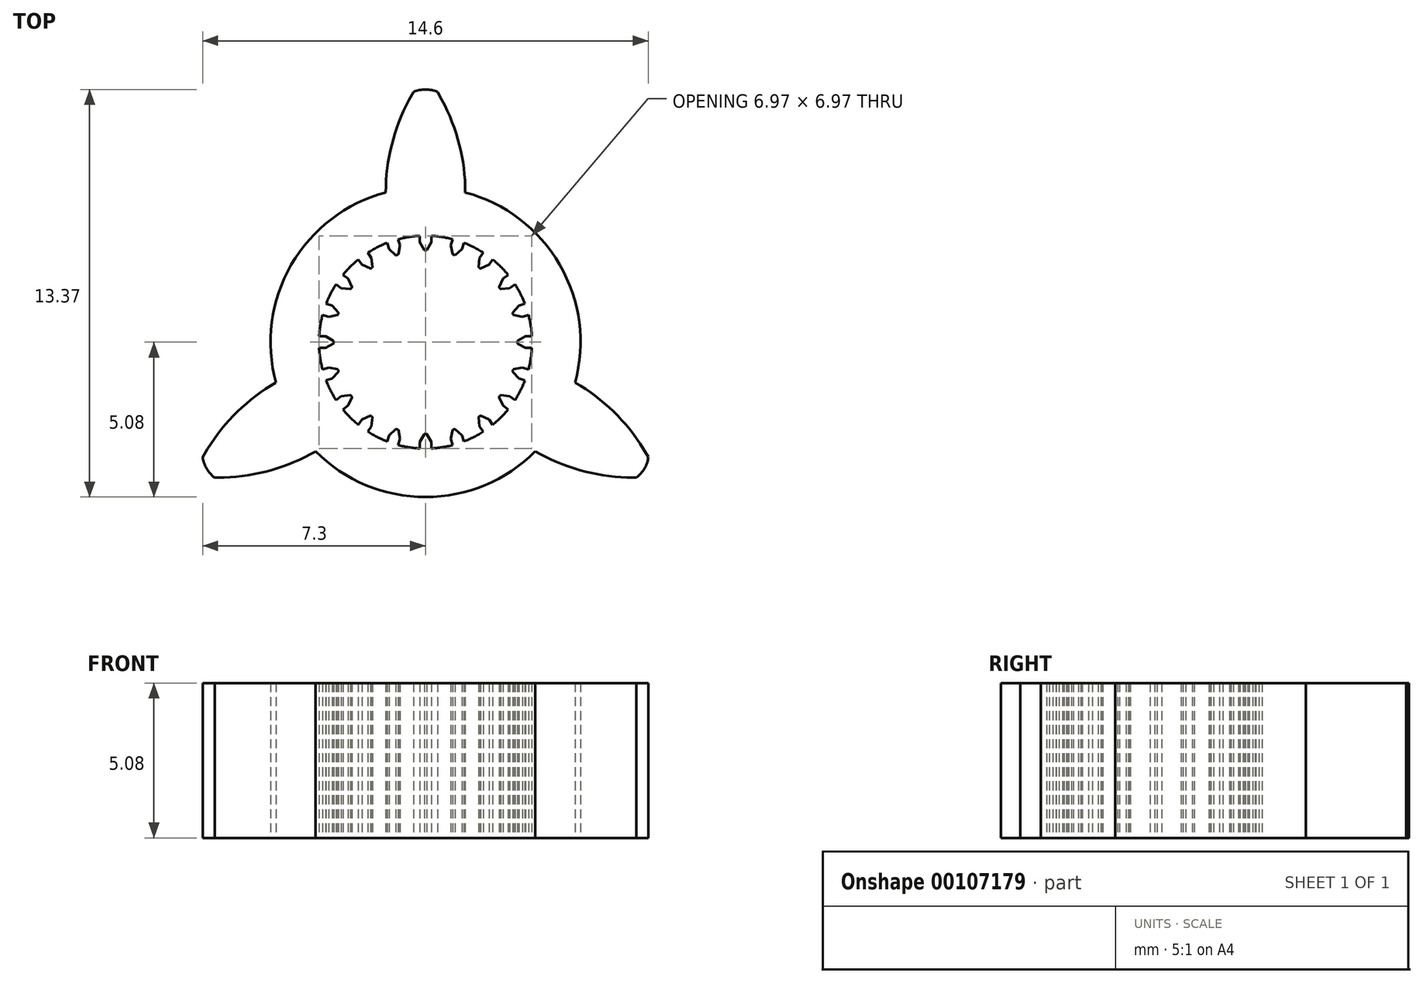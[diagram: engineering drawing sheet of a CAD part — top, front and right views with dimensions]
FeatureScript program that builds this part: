
annotation { "Feature Type Name" : "Feature", "Feature Type Description" : "" }
export const myFeature = defineFeature(function(context is Context, id is Id, definition is map)
    precondition{}
    {
        {
            var Q0;
            Q0=qCreatedBy(makeId("Top.planeOp"),FACE);
            var sketch = newSketch(context, id + "F0", { "sketchPlane" : qUnion([Q0])});
            skArc(sketch, "E0", {"start": v(-1.3, 4.9) * mm, "mid": v(-4.4, 2.54) * mm, "end": v(-4.9, -1.33) * mm});
            skLineSegment(sketch, "E1", {"start": v(-0.2, 3.49) * mm, "end": v(-0.2, 3.28) * mm});
            skArc(sketch, "E2", {"start": v(-0.04, 3.02) * mm, "mid": v(0, 3) * mm, "end": v(0.04, 3.02) * mm});
            skLineSegment(sketch, "E3", {"start": v(-0.2, 3.28) * mm, "end": v(-0.04, 3.02) * mm});
            skLineSegment(sketch, "E4.MirrorCS", {"start": v(0.2, 3.49) * mm, "end": v(0.2, 3.28) * mm});
            skLineSegment(sketch, "E5.MirrorCS", {"start": v(0.2, 3.28) * mm, "end": v(0.04, 3.02) * mm});
            skLineSegment(sketch, "E6.1.0", {"start": v(-0.9, 3.38) * mm, "end": v(-0.83, 3.18) * mm});
            skLineSegment(sketch, "E6.1.1", {"start": v(-0.83, 3.18) * mm, "end": v(-0.9, 2.88) * mm});
            skArc(sketch, "E6.1.2", {"start": v(-0.97, 2.85) * mm, "mid": v(-0.93, 2.86) * mm, "end": v(-0.9, 2.88) * mm});
            skLineSegment(sketch, "E6.1.3", {"start": v(-1.2, 3.06) * mm, "end": v(-0.97, 2.85) * mm});
            skLineSegment(sketch, "E6.1.4", {"start": v(-1.26, 3.26) * mm, "end": v(-1.2, 3.06) * mm});
            skLineSegment(sketch, "E6.2.0", {"start": v(-1.9, 2.93) * mm, "end": v(-1.77, 2.76) * mm});
            skLineSegment(sketch, "E6.2.1", {"start": v(-1.77, 2.76) * mm, "end": v(-1.74, 2.47) * mm});
            skArc(sketch, "E6.2.2", {"start": v(-1.8, 2.41) * mm, "mid": v(-1.77, 2.43) * mm, "end": v(-1.74, 2.47) * mm});
            skLineSegment(sketch, "E6.2.3", {"start": v(-2.08, 2.54) * mm, "end": v(-1.8, 2.41) * mm});
            skLineSegment(sketch, "E6.2.4", {"start": v(-2.2, 2.7) * mm, "end": v(-2.08, 2.54) * mm});
            skLineSegment(sketch, "E6.3.0", {"start": v(-2.7, 2.2) * mm, "end": v(-2.54, 2.08) * mm});
            skLineSegment(sketch, "E6.3.1", {"start": v(-2.54, 2.08) * mm, "end": v(-2.41, 1.8) * mm});
            skArc(sketch, "E6.3.2", {"start": v(-2.47, 1.74) * mm, "mid": v(-2.43, 1.77) * mm, "end": v(-2.41, 1.8) * mm});
            skLineSegment(sketch, "E6.3.3", {"start": v(-2.76, 1.77) * mm, "end": v(-2.47, 1.74) * mm});
            skLineSegment(sketch, "E6.3.4", {"start": v(-2.93, 1.9) * mm, "end": v(-2.76, 1.77) * mm});
            skLineSegment(sketch, "E6.4.0", {"start": v(-3.26, 1.26) * mm, "end": v(-3.06, 1.2) * mm});
            skLineSegment(sketch, "E6.4.1", {"start": v(-3.06, 1.2) * mm, "end": v(-2.85, 0.97) * mm});
            skArc(sketch, "E6.4.2", {"start": v(-2.88, 0.9) * mm, "mid": v(-2.86, 0.93) * mm, "end": v(-2.85, 0.97) * mm});
            skLineSegment(sketch, "E6.4.3", {"start": v(-3.18, 0.83) * mm, "end": v(-2.88, 0.9) * mm});
            skLineSegment(sketch, "E6.4.4", {"start": v(-3.38, 0.9) * mm, "end": v(-3.18, 0.83) * mm});
            skLineSegment(sketch, "E6.5.0", {"start": v(-3.49, 0.2) * mm, "end": v(-3.28, 0.2) * mm});
            skLineSegment(sketch, "E6.5.1", {"start": v(-3.28, 0.2) * mm, "end": v(-3.02, 0.04) * mm});
            skArc(sketch, "E6.5.2", {"start": v(-3.02, -0.04) * mm, "mid": v(-3, 0) * mm, "end": v(-3.02, 0.04) * mm});
            skLineSegment(sketch, "E6.5.3", {"start": v(-3.28, -0.2) * mm, "end": v(-3.02, -0.04) * mm});
            skLineSegment(sketch, "E6.5.4", {"start": v(-3.49, -0.2) * mm, "end": v(-3.28, -0.2) * mm});
            skLineSegment(sketch, "E6.6.0", {"start": v(-3.38, -0.9) * mm, "end": v(-3.18, -0.83) * mm});
            skLineSegment(sketch, "E6.6.1", {"start": v(-3.18, -0.83) * mm, "end": v(-2.88, -0.9) * mm});
            skArc(sketch, "E6.6.2", {"start": v(-2.85, -0.97) * mm, "mid": v(-2.86, -0.93) * mm, "end": v(-2.88, -0.9) * mm});
            skLineSegment(sketch, "E6.6.3", {"start": v(-3.06, -1.2) * mm, "end": v(-2.85, -0.97) * mm});
            skLineSegment(sketch, "E6.6.4", {"start": v(-3.26, -1.26) * mm, "end": v(-3.06, -1.2) * mm});
            skLineSegment(sketch, "E6.7.0", {"start": v(-2.93, -1.9) * mm, "end": v(-2.76, -1.77) * mm});
            skLineSegment(sketch, "E6.7.1", {"start": v(-2.76, -1.77) * mm, "end": v(-2.47, -1.74) * mm});
            skArc(sketch, "E6.7.2", {"start": v(-2.41, -1.8) * mm, "mid": v(-2.43, -1.77) * mm, "end": v(-2.47, -1.74) * mm});
            skLineSegment(sketch, "E6.7.3", {"start": v(-2.54, -2.08) * mm, "end": v(-2.41, -1.8) * mm});
            skLineSegment(sketch, "E6.7.4", {"start": v(-2.7, -2.2) * mm, "end": v(-2.54, -2.08) * mm});
            skLineSegment(sketch, "E6.8.0", {"start": v(-2.2, -2.7) * mm, "end": v(-2.08, -2.54) * mm});
            skLineSegment(sketch, "E6.8.1", {"start": v(-2.08, -2.54) * mm, "end": v(-1.8, -2.41) * mm});
            skArc(sketch, "E6.8.2", {"start": v(-1.74, -2.47) * mm, "mid": v(-1.77, -2.43) * mm, "end": v(-1.8, -2.41) * mm});
            skLineSegment(sketch, "E6.8.3", {"start": v(-1.77, -2.76) * mm, "end": v(-1.74, -2.47) * mm});
            skLineSegment(sketch, "E6.8.4", {"start": v(-1.9, -2.93) * mm, "end": v(-1.77, -2.76) * mm});
            skLineSegment(sketch, "E6.9.0", {"start": v(-1.26, -3.26) * mm, "end": v(-1.2, -3.06) * mm});
            skLineSegment(sketch, "E6.9.1", {"start": v(-1.2, -3.06) * mm, "end": v(-0.97, -2.85) * mm});
            skArc(sketch, "E6.9.2", {"start": v(-0.9, -2.88) * mm, "mid": v(-0.93, -2.86) * mm, "end": v(-0.97, -2.85) * mm});
            skLineSegment(sketch, "E6.9.3", {"start": v(-0.83, -3.18) * mm, "end": v(-0.9, -2.88) * mm});
            skLineSegment(sketch, "E6.9.4", {"start": v(-0.9, -3.38) * mm, "end": v(-0.83, -3.18) * mm});
            skLineSegment(sketch, "E6.10.0", {"start": v(-0.2, -3.49) * mm, "end": v(-0.2, -3.28) * mm});
            skLineSegment(sketch, "E6.10.1", {"start": v(-0.2, -3.28) * mm, "end": v(-0.04, -3.02) * mm});
            skArc(sketch, "E6.10.2", {"start": v(0.04, -3.02) * mm, "mid": v(0, -3) * mm, "end": v(-0.04, -3.02) * mm});
            skLineSegment(sketch, "E6.10.3", {"start": v(0.2, -3.28) * mm, "end": v(0.04, -3.02) * mm});
            skLineSegment(sketch, "E6.10.4", {"start": v(0.2, -3.49) * mm, "end": v(0.2, -3.28) * mm});
            skLineSegment(sketch, "E6.11.0", {"start": v(0.9, -3.38) * mm, "end": v(0.83, -3.18) * mm});
            skLineSegment(sketch, "E6.11.1", {"start": v(0.83, -3.18) * mm, "end": v(0.9, -2.88) * mm});
            skArc(sketch, "E6.11.2", {"start": v(0.97, -2.85) * mm, "mid": v(0.93, -2.86) * mm, "end": v(0.9, -2.88) * mm});
            skLineSegment(sketch, "E6.11.3", {"start": v(1.2, -3.06) * mm, "end": v(0.97, -2.85) * mm});
            skLineSegment(sketch, "E6.11.4", {"start": v(1.26, -3.26) * mm, "end": v(1.2, -3.06) * mm});
            skLineSegment(sketch, "E6.12.0", {"start": v(1.9, -2.93) * mm, "end": v(1.77, -2.76) * mm});
            skLineSegment(sketch, "E6.12.1", {"start": v(1.77, -2.76) * mm, "end": v(1.74, -2.47) * mm});
            skArc(sketch, "E6.12.2", {"start": v(1.8, -2.41) * mm, "mid": v(1.77, -2.43) * mm, "end": v(1.74, -2.47) * mm});
            skLineSegment(sketch, "E6.12.3", {"start": v(2.08, -2.54) * mm, "end": v(1.8, -2.41) * mm});
            skLineSegment(sketch, "E6.12.4", {"start": v(2.2, -2.7) * mm, "end": v(2.08, -2.54) * mm});
            skLineSegment(sketch, "E6.13.0", {"start": v(2.7, -2.2) * mm, "end": v(2.54, -2.08) * mm});
            skLineSegment(sketch, "E6.13.1", {"start": v(2.54, -2.08) * mm, "end": v(2.41, -1.8) * mm});
            skArc(sketch, "E6.13.2", {"start": v(2.47, -1.74) * mm, "mid": v(2.43, -1.77) * mm, "end": v(2.41, -1.8) * mm});
            skLineSegment(sketch, "E6.13.3", {"start": v(2.76, -1.77) * mm, "end": v(2.47, -1.74) * mm});
            skLineSegment(sketch, "E6.13.4", {"start": v(2.93, -1.9) * mm, "end": v(2.76, -1.77) * mm});
            skLineSegment(sketch, "E6.14.0", {"start": v(3.26, -1.26) * mm, "end": v(3.06, -1.2) * mm});
            skLineSegment(sketch, "E6.14.1", {"start": v(3.06, -1.2) * mm, "end": v(2.85, -0.97) * mm});
            skArc(sketch, "E6.14.2", {"start": v(2.88, -0.9) * mm, "mid": v(2.86, -0.93) * mm, "end": v(2.85, -0.97) * mm});
            skLineSegment(sketch, "E6.14.3", {"start": v(3.18, -0.83) * mm, "end": v(2.88, -0.9) * mm});
            skLineSegment(sketch, "E6.14.4", {"start": v(3.38, -0.9) * mm, "end": v(3.18, -0.83) * mm});
            skLineSegment(sketch, "E6.15.0", {"start": v(3.49, -0.2) * mm, "end": v(3.28, -0.2) * mm});
            skLineSegment(sketch, "E6.15.1", {"start": v(3.28, -0.2) * mm, "end": v(3.02, -0.04) * mm});
            skArc(sketch, "E6.15.2", {"start": v(3.02, 0.04) * mm, "mid": v(3, 0) * mm, "end": v(3.02, -0.04) * mm});
            skLineSegment(sketch, "E6.15.3", {"start": v(3.28, 0.2) * mm, "end": v(3.02, 0.04) * mm});
            skLineSegment(sketch, "E6.15.4", {"start": v(3.49, 0.2) * mm, "end": v(3.28, 0.2) * mm});
            skLineSegment(sketch, "E6.16.0", {"start": v(3.38, 0.9) * mm, "end": v(3.18, 0.83) * mm});
            skLineSegment(sketch, "E6.16.1", {"start": v(3.18, 0.83) * mm, "end": v(2.88, 0.9) * mm});
            skArc(sketch, "E6.16.2", {"start": v(2.85, 0.97) * mm, "mid": v(2.86, 0.93) * mm, "end": v(2.88, 0.9) * mm});
            skLineSegment(sketch, "E6.16.3", {"start": v(3.06, 1.2) * mm, "end": v(2.85, 0.97) * mm});
            skLineSegment(sketch, "E6.16.4", {"start": v(3.26, 1.26) * mm, "end": v(3.06, 1.2) * mm});
            skLineSegment(sketch, "E6.17.0", {"start": v(2.93, 1.9) * mm, "end": v(2.76, 1.77) * mm});
            skLineSegment(sketch, "E6.17.1", {"start": v(2.76, 1.77) * mm, "end": v(2.47, 1.74) * mm});
            skArc(sketch, "E6.17.2", {"start": v(2.41, 1.8) * mm, "mid": v(2.43, 1.77) * mm, "end": v(2.47, 1.74) * mm});
            skLineSegment(sketch, "E6.17.3", {"start": v(2.54, 2.08) * mm, "end": v(2.41, 1.8) * mm});
            skLineSegment(sketch, "E6.17.4", {"start": v(2.7, 2.2) * mm, "end": v(2.54, 2.08) * mm});
            skLineSegment(sketch, "E6.18.0", {"start": v(2.2, 2.7) * mm, "end": v(2.08, 2.54) * mm});
            skLineSegment(sketch, "E6.18.1", {"start": v(2.08, 2.54) * mm, "end": v(1.8, 2.41) * mm});
            skArc(sketch, "E6.18.2", {"start": v(1.74, 2.47) * mm, "mid": v(1.77, 2.43) * mm, "end": v(1.8, 2.41) * mm});
            skLineSegment(sketch, "E6.18.3", {"start": v(1.77, 2.76) * mm, "end": v(1.74, 2.47) * mm});
            skLineSegment(sketch, "E6.18.4", {"start": v(1.9, 2.93) * mm, "end": v(1.77, 2.76) * mm});
            skLineSegment(sketch, "E6.19.0", {"start": v(1.26, 3.26) * mm, "end": v(1.2, 3.06) * mm});
            skLineSegment(sketch, "E6.19.1", {"start": v(1.2, 3.06) * mm, "end": v(0.97, 2.85) * mm});
            skArc(sketch, "E6.19.2", {"start": v(0.9, 2.88) * mm, "mid": v(0.93, 2.86) * mm, "end": v(0.97, 2.85) * mm});
            skLineSegment(sketch, "E6.19.3", {"start": v(0.83, 3.18) * mm, "end": v(0.9, 2.88) * mm});
            skLineSegment(sketch, "E6.19.4", {"start": v(0.9, 3.38) * mm, "end": v(0.83, 3.18) * mm});
            skArc(sketch, "E7", {"start": v(0.2, 3.49) * mm, "mid": v(0.55, 3.45) * mm, "end": v(0.9, 3.38) * mm});
            skArc(sketch, "E8", {"start": v(3.38, 0.9) * mm, "mid": v(3.45, 0.55) * mm, "end": v(3.49, 0.2) * mm});
            skArc(sketch, "E9.1.0", {"start": v(2.93, 1.9) * mm, "mid": v(3.11, 1.59) * mm, "end": v(3.26, 1.26) * mm});
            skArc(sketch, "E9.2.0", {"start": v(2.2, 2.7) * mm, "mid": v(2.47, 2.47) * mm, "end": v(2.7, 2.2) * mm});
            skArc(sketch, "E9.3.0", {"start": v(1.26, 3.26) * mm, "mid": v(1.59, 3.11) * mm, "end": v(1.9, 2.93) * mm});
            skArc(sketch, "E9.5.0", {"start": v(-0.9, 3.38) * mm, "mid": v(-0.55, 3.45) * mm, "end": v(-0.2, 3.49) * mm});
            skArc(sketch, "E9.6.0", {"start": v(-1.9, 2.93) * mm, "mid": v(-1.59, 3.11) * mm, "end": v(-1.26, 3.26) * mm});
            skArc(sketch, "E9.7.0", {"start": v(-2.7, 2.2) * mm, "mid": v(-2.47, 2.47) * mm, "end": v(-2.2, 2.7) * mm});
            skArc(sketch, "E9.8.0", {"start": v(-3.26, 1.26) * mm, "mid": v(-3.11, 1.59) * mm, "end": v(-2.93, 1.9) * mm});
            skArc(sketch, "E9.9.0", {"start": v(-3.49, 0.2) * mm, "mid": v(-3.45, 0.55) * mm, "end": v(-3.38, 0.9) * mm});
            skArc(sketch, "E9.10.0", {"start": v(-3.38, -0.9) * mm, "mid": v(-3.45, -0.55) * mm, "end": v(-3.49, -0.2) * mm});
            skArc(sketch, "E9.11.0", {"start": v(-2.93, -1.9) * mm, "mid": v(-3.11, -1.59) * mm, "end": v(-3.26, -1.26) * mm});
            skArc(sketch, "E9.12.0", {"start": v(-2.2, -2.7) * mm, "mid": v(-2.47, -2.47) * mm, "end": v(-2.7, -2.2) * mm});
            skArc(sketch, "E9.13.0", {"start": v(-1.26, -3.26) * mm, "mid": v(-1.59, -3.11) * mm, "end": v(-1.9, -2.93) * mm});
            skArc(sketch, "E9.14.0", {"start": v(-0.2, -3.49) * mm, "mid": v(-0.55, -3.45) * mm, "end": v(-0.9, -3.38) * mm});
            skArc(sketch, "E9.15.0", {"start": v(0.9, -3.38) * mm, "mid": v(0.55, -3.45) * mm, "end": v(0.2, -3.49) * mm});
            skArc(sketch, "E9.16.0", {"start": v(1.9, -2.93) * mm, "mid": v(1.59, -3.11) * mm, "end": v(1.26, -3.26) * mm});
            skArc(sketch, "E9.17.0", {"start": v(2.7, -2.2) * mm, "mid": v(2.47, -2.47) * mm, "end": v(2.2, -2.7) * mm});
            skArc(sketch, "E9.18.0", {"start": v(3.26, -1.26) * mm, "mid": v(3.11, -1.59) * mm, "end": v(2.93, -1.9) * mm});
            skArc(sketch, "E9.19.0", {"start": v(3.49, -0.2) * mm, "mid": v(3.45, -0.55) * mm, "end": v(3.38, -0.9) * mm});
            skLineSegment(sketch, "E10", {"start": v(1.3, 4.9) * mm, "end": v(1.3, 4.92) * mm});
            skArc(sketch, "E11", {"start": v(0.4, 8.2) * mm, "mid": v(0.2, 8.27) * mm, "end": v(0, 8.29) * mm});
            skPoint(sketch, "E11.centerSnap0", {"position": v(0, 4.9) * mm});
            skLineSegment(sketch, "E12", {"start": v(0.54, 7.94) * mm, "end": v(0.4, 8.2) * mm});
            skPoint(sketch, "E13.visualSharp", {"position": v(1.3, 6.52) * mm});
            skArc(sketch, "E13.filletArc", {"start": v(1.3, 4.92) * mm, "mid": v(1.1, 6.47) * mm, "end": v(0.54, 7.94) * mm});
            skLineSegment(sketch, "E14.MirrorCS", {"start": v(-0.54, 7.94) * mm, "end": v(-0.4, 8.2) * mm});
            skLineSegment(sketch, "E15.MirrorCS", {"start": v(-1.3, 4.9) * mm, "end": v(-1.3, 4.92) * mm});
            skArc(sketch, "E16.MirrorCS", {"start": v(-0.4, 8.2) * mm, "mid": v(-0.2, 8.27) * mm, "end": v(0, 8.29) * mm});
            skPoint(sketch, "E17.MirrorP", {"position": v(-1.3, 6.52) * mm});
            skArc(sketch, "E18.MirrorCS", {"start": v(-1.3, 4.92) * mm, "mid": v(-1.1, 6.47) * mm, "end": v(-0.54, 7.94) * mm});
            skPoint(sketch, "E19.1.0", {"position": v(-4.25, -2.45) * mm});
            skPoint(sketch, "E19.1.1", {"position": v(-6.3, -2.13) * mm});
            skPoint(sketch, "E19.1.2", {"position": v(-5, -4.39) * mm});
            skArc(sketch, "E19.1.3", {"start": v(-3.6, -3.59) * mm, "mid": v(-5.05, -4.2) * mm, "end": v(-6.6, -4.43) * mm});
            skArc(sketch, "E19.1.4", {"start": v(-4.9, -1.33) * mm, "mid": v(-6.16, -2.28) * mm, "end": v(-7.14, -3.5) * mm});
            skPoint(sketch, "E19.1.5", {"position": v(-4.25, -2.45) * mm});
            skLineSegment(sketch, "E19.1.6", {"start": v(-7.14, -3.5) * mm, "end": v(-7.3, -3.77) * mm});
            skArc(sketch, "E19.1.7", {"start": v(-7.3, -3.77) * mm, "mid": v(-7.26, -3.96) * mm, "end": v(-7.18, -4.14) * mm});
            skArc(sketch, "E19.1.8", {"start": v(-6.91, -4.44) * mm, "mid": v(-7.06, -4.3) * mm, "end": v(-7.18, -4.14) * mm});
            skLineSegment(sketch, "E19.1.9", {"start": v(-6.6, -4.43) * mm, "end": v(-6.91, -4.44) * mm});
            skLineSegment(sketch, "E19.1.10", {"start": v(-4.9, -1.33) * mm, "end": v(-4.9, -1.33) * mm});
            skLineSegment(sketch, "E19.1.11", {"start": v(-3.6, -3.58) * mm, "end": v(-3.6, -3.59) * mm});
            skPoint(sketch, "E19.2.0", {"position": v(4.25, -2.45) * mm});
            skPoint(sketch, "E19.2.1", {"position": v(5, -4.39) * mm});
            skPoint(sketch, "E19.2.2", {"position": v(6.3, -2.13) * mm});
            skArc(sketch, "E19.2.3", {"start": v(4.9, -1.33) * mm, "mid": v(6.16, -2.28) * mm, "end": v(7.14, -3.5) * mm});
            skArc(sketch, "E19.2.4", {"start": v(3.6, -3.59) * mm, "mid": v(5.05, -4.2) * mm, "end": v(6.6, -4.43) * mm});
            skPoint(sketch, "E19.2.5", {"position": v(4.25, -2.45) * mm});
            skLineSegment(sketch, "E19.2.6", {"start": v(6.6, -4.43) * mm, "end": v(6.91, -4.44) * mm});
            skArc(sketch, "E19.2.7", {"start": v(6.91, -4.44) * mm, "mid": v(7.06, -4.3) * mm, "end": v(7.18, -4.14) * mm});
            skArc(sketch, "E19.2.8", {"start": v(7.3, -3.77) * mm, "mid": v(7.26, -3.96) * mm, "end": v(7.18, -4.14) * mm});
            skLineSegment(sketch, "E19.2.9", {"start": v(7.14, -3.5) * mm, "end": v(7.3, -3.77) * mm});
            skLineSegment(sketch, "E19.2.10", {"start": v(3.6, -3.58) * mm, "end": v(3.6, -3.59) * mm});
            skLineSegment(sketch, "E19.2.11", {"start": v(4.9, -1.33) * mm, "end": v(4.9, -1.33) * mm});
            skArc(sketch, "E20.trimOffspring", {"start": v(4.9, -1.33) * mm, "mid": v(4.4, 2.54) * mm, "end": v(1.3, 4.9) * mm});
            skArc(sketch, "E21.trimOffspring", {"start": v(-3.6, -3.58) * mm, "mid": v(0, -5.08) * mm, "end": v(3.6, -3.58) * mm});
            skSolve(sketch);
        }
        {
            var Q0;
            Q0=makeQuery(id+"F0.imprint","IMPRINT",FACE,{"disambiguationData":[TD([[makeQuery(id+"F0.imprint","IMPRINT",EDGE,{"derivedFrom":sQuery(id+"F0.wireOp",EDGE,"E0")}),1.0]])]});
            extrude(context, id + "F1", {"entities" : qUnion([Q0]), "depth" : 5.08 * mm});
        }
    });
